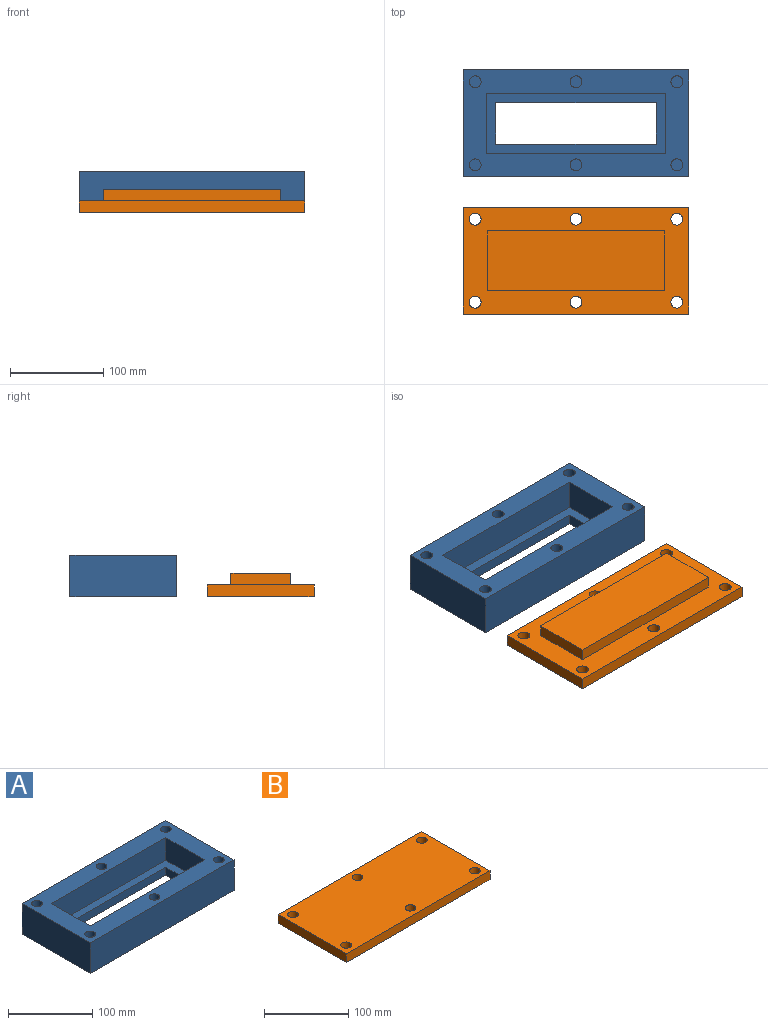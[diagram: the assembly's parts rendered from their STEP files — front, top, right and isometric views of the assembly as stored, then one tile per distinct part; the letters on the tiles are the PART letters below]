
ASSEMBLY  parts=2 mates=1
PART A: 27 faces, bbox 241.3x114.3x44.5 mm
  f0: plane 241.3x44.45mm, normal (0,1,0), area 10725.8mm2, adj f1,f3,f4,f5
  f1: plane 114.3x44.45mm, normal (-1,0,0), area 5080.6mm2, adj f0,f2,f4,f5
  f2: plane 241.3x44.45mm, normal (0,-1,0), area 10725.8mm2, adj f1,f3,f4,f5
  f3: plane 114.3x44.45mm, normal (1,0,0), area 5080.6mm2, adj f0,f2,f4,f5
  f4: plane 241.3x114.3mm, normal (0,0,1), area 14399.6mm2, adj f0,f1,f2,f3,f6,f7,f8,f9
  f5: plane 241.3x114.3mm, normal (0,0,-1), area 19959.6mm2, adj f0,f1,f2,f3,f11,f12,f13,f14
  f6: plane 64.77x33.02mm, normal (1,0,0), area 2138.7mm2, adj f4,f7,f9,f10
  f7: plane 191.77x33.02mm, normal (0,1,0), area 6332.2mm2, adj f4,f6,f8,f10
  f8: plane 64.77x33.02mm, normal (-1,0,0), area 2138.7mm2, adj f4,f7,f9,f10
  f9: plane 191.77x33.02mm, normal (0,-1,0), area 6332.2mm2, adj f4,f6,f8,f10
  f10: plane 191.77x64.77mm, normal (0,0,1), area 4800mm2, adj f6,f7,f8,f9,f11,f12,f13,f14
  f11: plane 44.45x11.43mm, normal (1,0,0), area 508.1mm2, adj f5,f10,f12,f14
  f12: plane 171.45x11.43mm, normal (0,-1,0), area 1959.7mm2, adj f5,f10,f11,f13
  f13: plane 44.45x11.43mm, normal (-1,0,0), area 508.1mm2, adj f5,f10,f12,f14
  f14: plane 171.45x11.43mm, normal (0,1,0), area 1959.7mm2, adj f5,f10,f11,f13
  f15: cylinder r=6.35mm len=25.4mm, axis (0,0,1), area 1013.4mm2, adj f4,f16
  f16: plane 12.7x12.7mm, normal (0,0,1), area 126.7mm2, adj f15
  f17: cylinder r=6.35mm len=25.4mm, axis (0,0,1), area 1013.4mm2, adj f4,f18
  f18: plane 12.7x12.7mm, normal (0,0,1), area 126.7mm2, adj f17
  f19: cylinder r=6.35mm len=25.4mm, axis (0,0,1), area 1013.4mm2, adj f4,f20
  f20: plane 12.7x12.7mm, normal (0,0,1), area 126.7mm2, adj f19
  f21: cylinder r=6.35mm len=25.4mm, axis (0,0,1), area 1013.4mm2, adj f4,f22
  f22: plane 12.7x12.7mm, normal (0,0,1), area 126.7mm2, adj f21
  f23: cylinder r=6.35mm len=25.4mm, axis (0,0,1), area 1013.4mm2, adj f4,f24
  f24: plane 12.7x12.7mm, normal (0,0,1), area 126.7mm2, adj f23
  f25: cylinder r=6.35mm len=25.4mm, axis (0,0,1), area 1013.4mm2, adj f4,f26
  f26: plane 12.7x12.7mm, normal (0,0,1), area 126.7mm2, adj f25
PART B: 17 faces, bbox 241.3x114.3x25.4 mm
  f0: plane 241.3x114.3mm, normal (0,0,-1), area 14723.8mm2, adj f1,f2,f3,f4,f6,f7,f8,f9
  f1: plane 241.3x12.7mm, normal (0,-1,0), area 3064.5mm2, adj f0,f2,f4,f5
  f2: plane 114.3x12.7mm, normal (1,0,0), area 1451.6mm2, adj f0,f1,f3,f5
  f3: plane 241.3x12.7mm, normal (0,1,0), area 3064.5mm2, adj f0,f2,f4,f5
  f4: plane 114.3x12.7mm, normal (-1,0,0), area 1451.6mm2, adj f0,f1,f3,f5
  f5: plane 241.3x114.3mm, normal (0,0,1), area 26820.5mm2, adj f1,f2,f3,f4,f11,f12,f13,f14
  f6: plane 63.5x12.7mm, normal (-1,0,0), area 806.5mm2, adj f0,f7,f9,f10
  f7: plane 190.5x12.7mm, normal (0,1,0), area 2419.3mm2, adj f0,f6,f8,f10
  f8: plane 63.5x12.7mm, normal (1,0,0), area 806.5mm2, adj f0,f7,f9,f10
  f9: plane 190.5x12.7mm, normal (0,-1,0), area 2419.3mm2, adj f0,f6,f8,f10
  f10: plane 190.5x63.5mm, normal (0,0,-1), area 12096.8mm2, adj f6,f7,f8,f9
  f11: cylinder r=6.35mm len=12.7mm, axis (0,0,1), area 506.7mm2, adj f0,f5
  f12: cylinder r=6.35mm len=12.7mm, axis (0,0,1), area 506.7mm2, adj f0,f5
  f13: cylinder r=6.35mm len=12.7mm, axis (0,0,1), area 506.7mm2, adj f0,f5
  f14: cylinder r=6.35mm len=12.7mm, axis (0,0,1), area 506.7mm2, adj f0,f5
  f15: cylinder r=6.35mm len=12.7mm, axis (0,0,1), area 506.7mm2, adj f0,f5
  f16: cylinder r=6.35mm len=12.7mm, axis (0,0,1), area 506.7mm2, adj f0,f5
PLACE A t=(-143.01,47.91,-26.79)mm fixed
PLACE B rot(axis=(0,-1,0),180deg) t=(-143.01,-99.05,-14.09)mm
MATE slider A.f2 <-> B.f3  axis (0,-1,0) through (-263.66,-9.24,-26.79)mm
